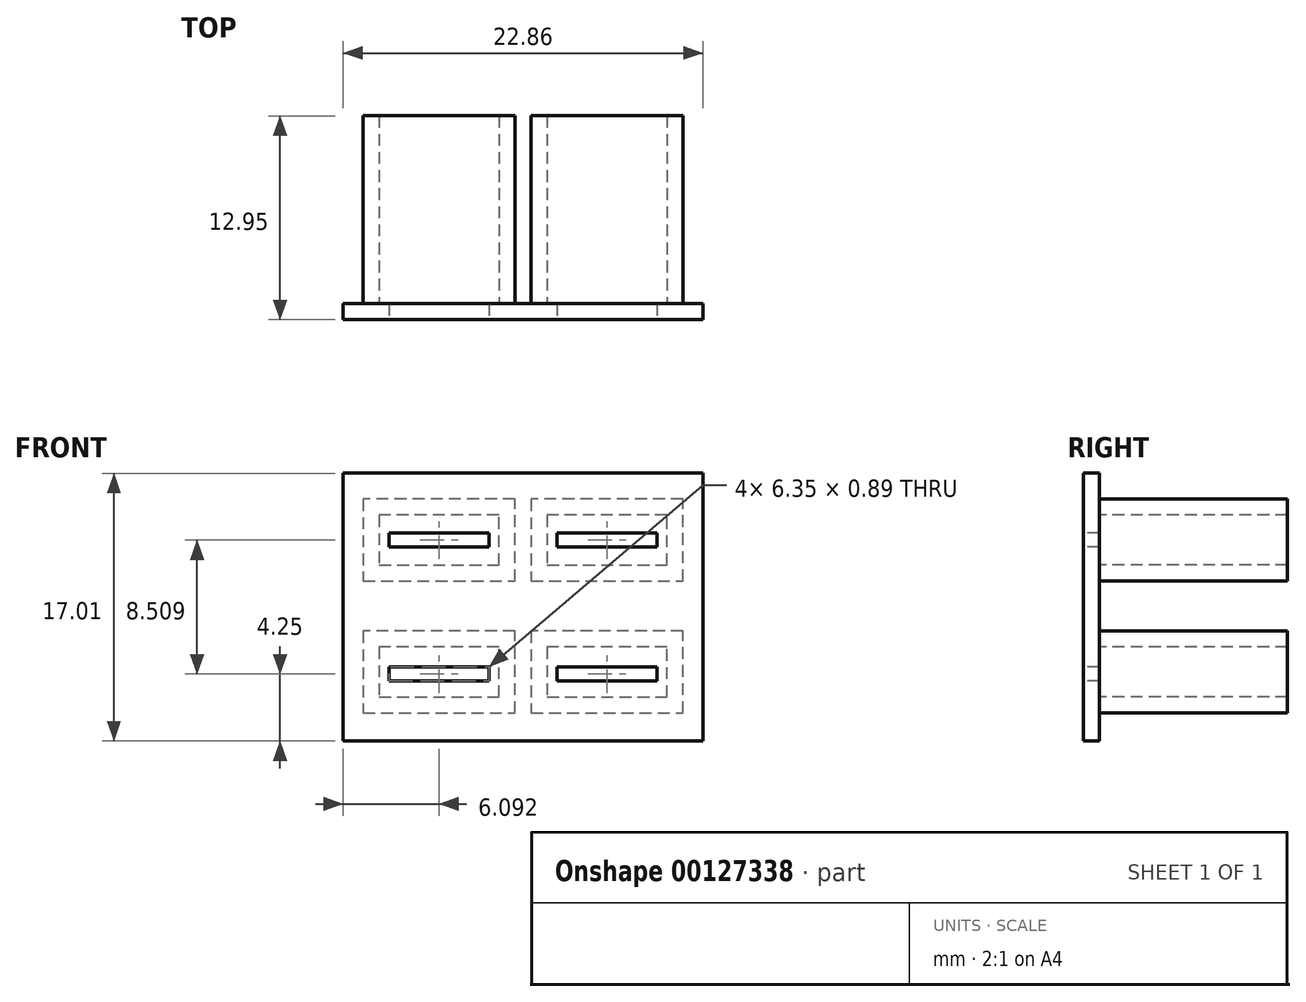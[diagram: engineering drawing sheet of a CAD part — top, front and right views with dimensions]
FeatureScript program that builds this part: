
annotation { "Feature Type Name" : "Feature", "Feature Type Description" : "" }
export const myFeature = defineFeature(function(context is Context, id is Id, definition is map)
    precondition{}
    {
        {
            var Q0;
            Q0=qCreatedBy(makeId("Front.planeOp"),FACE);
            var sketch = newSketch(context, id + "F0", { "sketchPlane" : qUnion([Q0])});
            skLineSegment(sketch, "E0", {"start": v(-22.83, 35) * mm, "end": v(-22.83, 12.13) * mm});
            skLineSegment(sketch, "E1", {"start": v(-22.83, 12.13) * mm, "end": v(2.57, 12.13) * mm});
            skLineSegment(sketch, "E2", {"start": v(2.57, 12.13) * mm, "end": v(2.57, 35) * mm});
            skLineSegment(sketch, "E3", {"start": v(2.57, 35) * mm, "end": v(-22.83, 35) * mm});
            skSolve(sketch);
        }
        {
            var Q0;
            Q0 = qSketchRegion(id + "F0", true);
            extrude(context, id + "F1", {"entities" : qUnion([Q0]), "oppositeDirection" : true, "depth" : 1.02 * mm});
        }
        {
            var Q0;
            Q0=makeQuery(id+"F1.opExtrude","CAP_FACE",FACE,{"disambiguationData":[OSD([sQuery(id+"F0.wireOp",EDGE,"E0"),sQuery(id+"F0.wireOp",EDGE,"E1"),sQuery(id+"F0.wireOp",EDGE,"E2"),sQuery(id+"F0.wireOp",EDGE,"E3")])],"isStart":true});
            var sketch = newSketch(context, id + "F2", { "sketchPlane" : qUnion([Q0])});
            skLineSegment(sketch, "E4", {"start": v(-17.37, 28.13) * mm, "end": v(-17.37, 27.24) * mm});
            skLineSegment(sketch, "E5", {"start": v(-17.37, 27.24) * mm, "end": v(-11.02, 27.24) * mm});
            skLineSegment(sketch, "E6", {"start": v(-11.02, 27.24) * mm, "end": v(-11.02, 28.13) * mm});
            skLineSegment(sketch, "E7", {"start": v(-11.02, 28.13) * mm, "end": v(-17.37, 28.13) * mm});
            skLineSegment(sketch, "E8", {"start": v(-6.7, 28.13) * mm, "end": v(-6.7, 27.24) * mm});
            skLineSegment(sketch, "E9", {"start": v(-6.7, 27.24) * mm, "end": v(-0.36, 27.24) * mm});
            skLineSegment(sketch, "E10", {"start": v(-0.36, 27.24) * mm, "end": v(-0.36, 28.13) * mm});
            skLineSegment(sketch, "E11", {"start": v(-0.36, 28.13) * mm, "end": v(-6.7, 28.13) * mm});
            skLineSegment(sketch, "E12", {"start": v(-17.37, 19.62) * mm, "end": v(-17.37, 18.74) * mm});
            skLineSegment(sketch, "E13", {"start": v(-17.37, 18.74) * mm, "end": v(-11.02, 18.74) * mm});
            skLineSegment(sketch, "E14", {"start": v(-11.02, 18.74) * mm, "end": v(-11.02, 19.62) * mm});
            skLineSegment(sketch, "E15", {"start": v(-11.02, 19.62) * mm, "end": v(-17.37, 19.62) * mm});
            skLineSegment(sketch, "E16", {"start": v(-6.7, 19.62) * mm, "end": v(-6.7, 18.74) * mm});
            skLineSegment(sketch, "E17", {"start": v(-6.7, 18.74) * mm, "end": v(-0.36, 18.74) * mm});
            skLineSegment(sketch, "E18", {"start": v(-0.36, 18.74) * mm, "end": v(-0.36, 19.62) * mm});
            skLineSegment(sketch, "E19", {"start": v(-0.36, 19.62) * mm, "end": v(-6.7, 19.62) * mm});
            skSolve(sketch);
        }
        {
            var Q0;
            Q0 = qSketchRegion(id + "F2", true);
            extrude(context, id + "F3", {"entities" : qUnion([Q0]), "operationType" : NewBodyOperationType.REMOVE, "oppositeDirection" : true, "depth" : 25.4 * mm});
        }
        {
            var Q0;
            Q0=makeQuery(id+"F1.opExtrude","CAP_FACE",FACE,{"disambiguationData":[OSD([sQuery(id+"F0.wireOp",EDGE,"E0"),sQuery(id+"F0.wireOp",EDGE,"E1"),sQuery(id+"F0.wireOp",EDGE,"E2"),sQuery(id+"F0.wireOp",EDGE,"E3")])],"isStart":true});
            var sketch = newSketch(context, id + "F4", { "sketchPlane" : qUnion([Q0])});
            skLineSegment(sketch, "E20", {"start": v(-18, 29.28) * mm, "end": v(-18, 26.1) * mm});
            skLineSegment(sketch, "E21", {"start": v(-18, 26.1) * mm, "end": v(-10.39, 26.1) * mm});
            skLineSegment(sketch, "E22", {"start": v(-10.39, 26.1) * mm, "end": v(-10.39, 29.28) * mm});
            skLineSegment(sketch, "E23", {"start": v(-10.39, 29.28) * mm, "end": v(-18, 29.28) * mm});
            skLineSegment(sketch, "E24", {"start": v(-7.34, 29.28) * mm, "end": v(-7.34, 26.1) * mm});
            skLineSegment(sketch, "E25", {"start": v(-7.34, 26.1) * mm, "end": v(0.28, 26.1) * mm});
            skLineSegment(sketch, "E26", {"start": v(0.28, 26.1) * mm, "end": v(0.28, 29.28) * mm});
            skLineSegment(sketch, "E27", {"start": v(0.28, 29.28) * mm, "end": v(-7.34, 29.28) * mm});
            skLineSegment(sketch, "E28", {"start": v(-19.02, 30.3) * mm, "end": v(-19.02, 25.09) * mm});
            skLineSegment(sketch, "E29", {"start": v(-19.02, 25.09) * mm, "end": v(-9.37, 25.09) * mm});
            skLineSegment(sketch, "E30", {"start": v(-9.37, 25.09) * mm, "end": v(-9.37, 30.3) * mm});
            skLineSegment(sketch, "E31", {"start": v(-9.37, 30.3) * mm, "end": v(-19.02, 30.3) * mm});
            skLineSegment(sketch, "E32", {"start": v(-8.36, 30.3) * mm, "end": v(-8.36, 25.09) * mm});
            skLineSegment(sketch, "E33", {"start": v(-8.36, 25.09) * mm, "end": v(1.3, 25.09) * mm});
            skLineSegment(sketch, "E34", {"start": v(1.3, 25.09) * mm, "end": v(1.3, 30.3) * mm});
            skLineSegment(sketch, "E35", {"start": v(1.3, 30.3) * mm, "end": v(-8.36, 30.3) * mm});
            skLineSegment(sketch, "E36.0.1.0", {"start": v(-9.37, 21.91) * mm, "end": v(-19.02, 21.91) * mm});
            skLineSegment(sketch, "E36.0.1.1", {"start": v(-10.39, 20.9) * mm, "end": v(-18, 20.9) * mm});
            skLineSegment(sketch, "E36.0.1.2", {"start": v(-10.39, 17.72) * mm, "end": v(-10.39, 20.9) * mm});
            skLineSegment(sketch, "E36.0.1.3", {"start": v(-18, 17.72) * mm, "end": v(-10.39, 17.72) * mm});
            skLineSegment(sketch, "E36.0.1.4", {"start": v(-18, 20.9) * mm, "end": v(-18, 17.72) * mm});
            skLineSegment(sketch, "E36.0.1.5", {"start": v(-9.37, 16.7) * mm, "end": v(-9.37, 21.91) * mm});
            skLineSegment(sketch, "E36.0.1.6", {"start": v(-19.02, 16.7) * mm, "end": v(-9.37, 16.7) * mm});
            skLineSegment(sketch, "E36.0.1.7", {"start": v(-19.02, 21.91) * mm, "end": v(-19.02, 16.7) * mm});
            skLineSegment(sketch, "E36.0.1.8", {"start": v(-7.34, 17.72) * mm, "end": v(0.28, 17.72) * mm});
            skLineSegment(sketch, "E36.0.1.9", {"start": v(0.28, 20.9) * mm, "end": v(-7.34, 20.9) * mm});
            skLineSegment(sketch, "E36.0.1.10", {"start": v(-7.34, 20.9) * mm, "end": v(-7.34, 17.72) * mm});
            skLineSegment(sketch, "E36.0.1.11", {"start": v(0.28, 17.72) * mm, "end": v(0.28, 20.9) * mm});
            skLineSegment(sketch, "E36.0.1.12", {"start": v(1.3, 16.7) * mm, "end": v(1.3, 21.91) * mm});
            skLineSegment(sketch, "E36.0.1.13", {"start": v(1.3, 21.91) * mm, "end": v(-8.36, 21.91) * mm});
            skLineSegment(sketch, "E36.0.1.14", {"start": v(-8.36, 21.91) * mm, "end": v(-8.36, 16.7) * mm});
            skLineSegment(sketch, "E36.0.1.15", {"start": v(-8.36, 16.7) * mm, "end": v(1.3, 16.7) * mm});
            skLineSegment(sketch, "E36.direction1", {"start": v(-19.02, 30.3) * mm, "end": v(6.38, 30.3) * mm, "construction": true});
            skLineSegment(sketch, "E36.direction2", {"start": v(-19.02, 30.3) * mm, "end": v(-19.02, 21.91) * mm, "construction": true});
            skSolve(sketch);
        }
        {
            var Q0;
            Q0 = qSketchRegion(id + "F4", true);
            extrude(context, id + "F5", {"entities" : qUnion([Q0]), "operationType" : NewBodyOperationType.ADD, "oppositeDirection" : true, "depth" : 12.95 * mm});
        }
        {
            var Q0;
            Q0=makeQuery(id+"F1.opExtrude","CAP_FACE",FACE,{"disambiguationData":[OSD([sQuery(id+"F0.wireOp",EDGE,"E0"),sQuery(id+"F0.wireOp",EDGE,"E1"),sQuery(id+"F0.wireOp",EDGE,"E2"),sQuery(id+"F0.wireOp",EDGE,"E3")])],"isStart":true});
            var sketch = newSketch(context, id + "F6", { "sketchPlane" : qUnion([Q0])});
            skLineSegment(sketch, "E37", {"start": v(-22.83, 14.93) * mm, "end": v(2.57, 14.93) * mm});
            skLineSegment(sketch, "E38", {"start": v(2.57, 14.93) * mm, "end": v(2.57, 12.13) * mm});
            skLineSegment(sketch, "E39", {"start": v(2.57, 12.13) * mm, "end": v(-22.83, 12.13) * mm});
            skLineSegment(sketch, "E40", {"start": v(-22.83, 12.13) * mm, "end": v(-22.83, 14.93) * mm});
            skLineSegment(sketch, "E41", {"start": v(-22.83, 35) * mm, "end": v(-22.83, 31.94) * mm});
            skLineSegment(sketch, "E42", {"start": v(-22.83, 31.94) * mm, "end": v(2.57, 31.94) * mm});
            skLineSegment(sketch, "E43", {"start": v(2.57, 31.94) * mm, "end": v(2.57, 35) * mm});
            skLineSegment(sketch, "E44", {"start": v(2.57, 35) * mm, "end": v(-22.83, 35) * mm});
            skSolve(sketch);
        }
        {
            var Q0;
            Q0 = qSketchRegion(id + "F6", true);
            extrude(context, id + "F7", {"entities" : qUnion([Q0]), "operationType" : NewBodyOperationType.REMOVE, "endBound" : BoundingType.THROUGH_ALL, "oppositeDirection" : true, "depth" : 25.4 * mm});
        }
        {
            var Q0;
            Q0=makeQuery(id+"F1.opExtrude","CAP_FACE",FACE,{"disambiguationData":[OSD([sQuery(id+"F0.wireOp",EDGE,"E0"),sQuery(id+"F0.wireOp",EDGE,"E1"),sQuery(id+"F0.wireOp",EDGE,"E2"),sQuery(id+"F0.wireOp",EDGE,"E3")])],"isStart":true});
            var sketch = newSketch(context, id + "F8", { "sketchPlane" : qUnion([Q0])});
            skLineSegment(sketch, "E45", {"start": v(-22.83, 31.94) * mm, "end": v(-22.83, 14.93) * mm});
            skLineSegment(sketch, "E46", {"start": v(-22.83, 31.94) * mm, "end": v(-20.3, 31.94) * mm});
            skLineSegment(sketch, "E47", {"start": v(-20.3, 31.94) * mm, "end": v(-20.3, 14.93) * mm});
            skLineSegment(sketch, "E48", {"start": v(-20.3, 14.93) * mm, "end": v(-22.83, 14.93) * mm});
            skSolve(sketch);
        }
        {
            var Q0;
            Q0 = qSketchRegion(id + "F8", true);
            extrude(context, id + "F9", {"entities" : qUnion([Q0]), "operationType" : NewBodyOperationType.REMOVE, "oppositeDirection" : true, "depth" : 25.4 * mm});
        }
    });
